# Revit family: Faucet-Kitchen-American_Standard-Studio_S-4803350_Series
name_source: partatom
category: Plumbing Fixtures
revit_build: Autodesk Revit 2014 (Build: 20130308_1515(x64)
units: mm (PartAtom-declared; Revit-internal decimal feet)

## types (3) — shared parameters
ADA Compliant = Yes
Assembly Code = D2020300
CW Connection = Yes
CWFU = 1.5
Cold Water Connection Diameter = 3/8"
Default Elevation = 0"
Description = Studio® S Semi Pro Pull-Down Dual Spray Kitchen Faucet with Spring Spout
HW Connection = Yes
HWFU = 1.5
Height = 20 3/8"
Hot Water Connection Diameter = 0"
Installation Type = Deck Mounted
Length = 8 1/2"
Manufacturer = American Standard
Price = Prices may vary. Please consult Manufacturer Representative for most up-to-date price list.
URL = https://www.americanstandard-us.com
Vent Connection = No
WFU = 2
Warranty Information = Limited Lifetime Function and Finish Warranty
Waste Connection = No
Width = 2 3/16"

## per-type parameters (varying)
| type | Finish | Material |
| 4803350.002 | Brass-American Standard-002-Polished Chrome | Brass-American Standard-002-Polished Chrome |
| 4803350.075 | Brass-American Standard-075-Stainless Steel | Brass-American Standard-075-Stainless Steel |
| 4803350.243 | Metal-American Standard-243-Matte Black | Metal-American Standard-243-Matte Black |

note: column(s) folded — value = type name in every type: Model

## geometry (parser evidence)
native form markers: Sweep x1
no freeform markers — native parametric forms only
